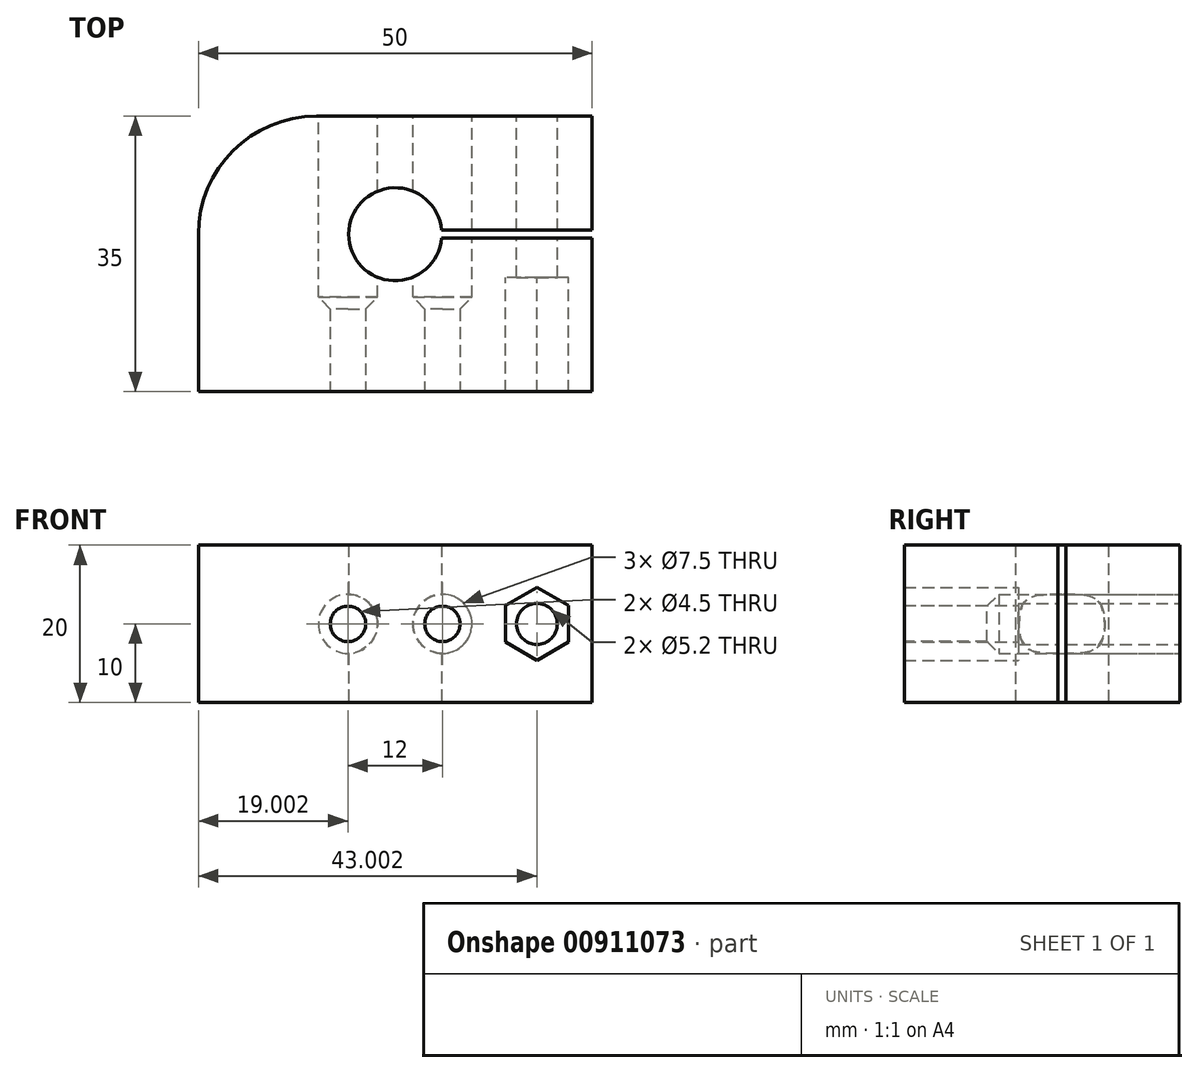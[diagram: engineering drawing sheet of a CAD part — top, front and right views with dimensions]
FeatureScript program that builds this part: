
annotation { "Feature Type Name" : "Feature", "Feature Type Description" : "" }
export const myFeature = defineFeature(function(context is Context, id is Id, definition is map)
    precondition{}
    {
        {
            var Q0;
            Q0=qCreatedBy(makeId("Top.planeOp"),FACE);
            var sketch = newSketch(context, id + "F0", { "sketchPlane" : qUnion([Q0])});
            skLineSegment(sketch, "E0.bottom", {"start": v(0.3, 0) * mm, "end": v(50.3, 0) * mm});
            skLineSegment(sketch, "E0.top", {"start": v(0.3, 35) * mm, "end": v(50.3, 35) * mm});
            skLineSegment(sketch, "E0.left", {"start": v(0.3, 0) * mm, "end": v(0.3, 35) * mm});
            skLineSegment(sketch, "E0.right", {"start": v(50.3, 0) * mm, "end": v(50.3, 19.5) * mm});
            skArc(sketch, "E1", {"start": v(31.17, 20.5) * mm, "mid": v(19.4, 20) * mm, "end": v(31.17, 19.5) * mm});
            skLineSegment(sketch, "E2.bottom", {"start": v(31.17, 19.5) * mm, "end": v(50.3, 19.5) * mm});
            skLineSegment(sketch, "E2.top", {"start": v(31.17, 20.5) * mm, "end": v(50.3, 20.5) * mm});
            skLineSegment(sketch, "E3.trimOffspring", {"start": v(50.3, 20.5) * mm, "end": v(50.3, 35) * mm});
            skSolve(sketch);
        }
        {
            var Q0;
            Q0=makeQuery(id+"F0.imprint","IMPRINT",FACE,{"disambiguationData":[TD([[makeQuery(id+"F0.imprint","IMPRINT",EDGE,{"derivedFrom":sQuery(id+"F0.wireOp",EDGE,"E0.bottom")}),1.0]])]});
            extrude(context, id + "F1", {"entities" : qUnion([Q0]), "depth" : 20 * mm, "offsetDistance" : 25 * mm});
        }
        {
            var Q0;
            Q0=makeQuery(id+"F1.opExtrude","SWEPT_FACE",FACE,{"disambiguationData":[OSD([sQuery(id+"F0.wireOp",EDGE,"E2.bottom")])]});
            var sketch = newSketch(context, id + "F2", { "sketchPlane" : qUnion([Q0])});
            skCircle(sketch, "E4.cCircle", {"center": v(-43.3, 10) * mm, "radius": 4 * mm, "construction": true});
            skLineSegment(sketch, "E4.0", {"start": v(-39.3, 12.3) * mm, "end": v(-39.3, 7.7) * mm});
            skLineSegment(sketch, "E4.1", {"start": v(-39.3, 7.7) * mm, "end": v(-43.3, 5.38) * mm});
            skLineSegment(sketch, "E4.2", {"start": v(-43.3, 5.38) * mm, "end": v(-47.3, 7.7) * mm});
            skLineSegment(sketch, "E4.3", {"start": v(-47.3, 7.7) * mm, "end": v(-47.3, 12.3) * mm});
            skLineSegment(sketch, "E4.4", {"start": v(-47.3, 12.3) * mm, "end": v(-43.3, 14.62) * mm});
            skLineSegment(sketch, "E4.5", {"start": v(-43.3, 14.62) * mm, "end": v(-39.3, 12.3) * mm});
            skPoint(sketch, "E4.0.midPoint", {"position": v(-39.3, 10) * mm});
            skSolve(sketch);
        }
        {
            var Q0;
            Q0=makeQuery(id+"F2.imprint","IMPRINT",FACE,{"disambiguationData":[TD([[makeQuery(id+"F2.imprint","IMPRINT",EDGE,{"derivedFrom":sQuery(id+"F2.wireOp",EDGE,"E4.0")}),-1.0]])]});
            extrude(context, id + "F3", {"entities" : qUnion([Q0]), "operationType" : NewBodyOperationType.REMOVE, "endBound" : BoundingType.UP_TO_NEXT, "oppositeDirection" : true, "depth" : 25 * mm, "offsetDistance" : 25 * mm, "hasSecondDirection" : true, "secondDirectionOppositeDirection" : true, "secondDirectionDepth" : 5 * mm});
        }
        {
            var Q0;
            Q0=makeQuery(id+"F1.opExtrude","SWEPT_FACE",FACE,{"disambiguationData":[OSD([sQuery(id+"F0.wireOp",EDGE,"E2.top")])]});
            var sketch = newSketch(context, id + "F4", { "sketchPlane" : qUnion([Q0])});
            skCircle(sketch, "E5", {"center": v(43.3, 10) * mm, "radius": 2.6 * mm});
            skSolve(sketch);
        }
        {
            var Q0;
            Q0=makeQuery(id+"F4.imprint","IMPRINT",FACE,{"disambiguationData":[TD([[makeQuery(id+"F4.imprint","IMPRINT",EDGE,{"derivedFrom":sQuery(id+"F4.wireOp",EDGE,"E5")}),1.0]])]});
            extrude(context, id + "F5", {"entities" : qUnion([Q0]), "operationType" : NewBodyOperationType.REMOVE, "endBound" : BoundingType.SYMMETRIC, "depth" : 50 * mm, "offsetDistance" : 25 * mm, "hasSecondDirection" : true, "secondDirectionOppositeDirection" : true, "secondDirectionDepth" : 25 * mm});
        }
        {
            var Q0;
            Q0=makeQuery(id+"F1.opExtrude","SWEPT_FACE",FACE,{"disambiguationData":[OSD([sQuery(id+"F0.wireOp",EDGE,"E0.bottom")])]});
            var sketch = newSketch(context, id + "F6", { "sketchPlane" : qUnion([Q0])});
            skLineSegment(sketch, "E6", {"start": v(0.3, 10) * mm, "end": v(50.3, 10) * mm, "construction": true});
            skCircle(sketch, "E7", {"center": v(19.3, 10) * mm, "radius": 2.25 * mm});
            skLineSegment(sketch, "E8", {"start": v(25.3, 20) * mm, "end": v(25.3, 0) * mm, "construction": true});
            skCircle(sketch, "E9.MirrorC", {"center": v(31.3, 10) * mm, "radius": 2.25 * mm});
            skSolve(sketch);
        }
        {
            var Q0;
            Q0 = qSketchRegion(id + "F6", true);
            extrude(context, id + "F7", {"entities" : qUnion([Q0]), "operationType" : NewBodyOperationType.REMOVE, "endBound" : BoundingType.THROUGH_ALL, "oppositeDirection" : true, "depth" : 25 * mm, "offsetDistance" : 25 * mm});
        }
        {
            var Q0;
            Q0=makeQuery(id+"F1.opExtrude","SWEPT_FACE",FACE,{"disambiguationData":[OSD([sQuery(id+"F0.wireOp",EDGE,"E0.top")])]});
            var sketch = newSketch(context, id + "F8", { "sketchPlane" : qUnion([Q0])});
            skCircle(sketch, "E10", {"center": v(-31.3, 10) * mm, "radius": 2.25 * mm, "construction": true});
            skPoint(sketch, "E10.first.point", {"position": v(-31.8, 12.2) * mm});
            skPoint(sketch, "E10.second.point", {"position": v(-29.69, 11.58) * mm});
            skPoint(sketch, "E10.third.point", {"position": v(-33.32, 10.98) * mm});
            skCircle(sketch, "E11", {"center": v(-19.3, 10) * mm, "radius": 2.25 * mm, "construction": true});
            skPoint(sketch, "E11.first.point", {"position": v(-19.49, 12.24) * mm});
            skPoint(sketch, "E11.second.point", {"position": v(-18.02, 11.85) * mm});
            skPoint(sketch, "E11.third.point", {"position": v(-17.27, 9.02) * mm});
            skCircle(sketch, "E12", {"center": v(-31.3, 10) * mm, "radius": 3.75 * mm});
            skCircle(sketch, "E13", {"center": v(-19.3, 10) * mm, "radius": 3.75 * mm});
            skSolve(sketch);
        }
        {
            var Q0;
            Q0 = qSketchRegion(id + "F8", true);
            extrude(context, id + "F9", {"entities" : qUnion([Q0]), "operationType" : NewBodyOperationType.REMOVE, "oppositeDirection" : true, "depth" : 21 * mm, "offsetDistance" : 25 * mm});
        }
        {
            var Q0;
            Q0=makeQuery(id+"F9.boolean.opBoolean","INTERSECT",EDGE,{"derivedFrom":[makeQuery(id+"F7.boolean.opBoolean","COPY",FACE,{"disambiguationData":[TD([makeQuery(id+"F1.opExtrude","SWEPT_FACE",FACE,{"disambiguationData":[OSD([sQuery(id+"F0.wireOp",EDGE,"E0.bottom")])]})])],"derivedFrom":makeQuery(id+"F7.opExtrude","SWEPT_FACE",FACE,{"disambiguationData":[OSD([sQuery(id+"F6.wireOp",EDGE,"E9.MirrorC")])]})}),makeQuery(id+"F9.opExtrude","CAP_FACE",FACE,{"disambiguationData":[OSD([sQuery(id+"F8.wireOp",EDGE,"E12")])],"isStart":false})]});
            var Q1;
            Q1=makeQuery(id+"F9.boolean.opBoolean","INTERSECT",EDGE,{"derivedFrom":[makeQuery(id+"F7.boolean.opBoolean","COPY",FACE,{"derivedFrom":makeQuery(id+"F7.opExtrude","SWEPT_FACE",FACE,{"disambiguationData":[OSD([sQuery(id+"F6.wireOp",EDGE,"E7")])]})}),makeQuery(id+"F9.opExtrude","CAP_FACE",FACE,{"disambiguationData":[OSD([sQuery(id+"F8.wireOp",EDGE,"E13")])],"isStart":false})]});
            chamfer(context, id + "F10", {"entities" : qUnion([Q0, Q1]), "width" : 3.5 * mm, "tangentPropagation" : true});
        }
        {
            var Q0;
            Q0=makeQuery(id+"F1.opExtrude","SWEPT_EDGE",EDGE,{"disambiguationData":[OSD([sQuery(id+"F0.wireOp",EDGE,"E0.top"),sQuery(id+"F0.wireOp",EDGE,"E0.left")])]});
            fillet(context, id + "F11", {"entities" : qUnion([Q0]), "radius" : 15 * mm, "tangentPropagation" : true, "allowEdgeOverflow" : false});
        }
    });
